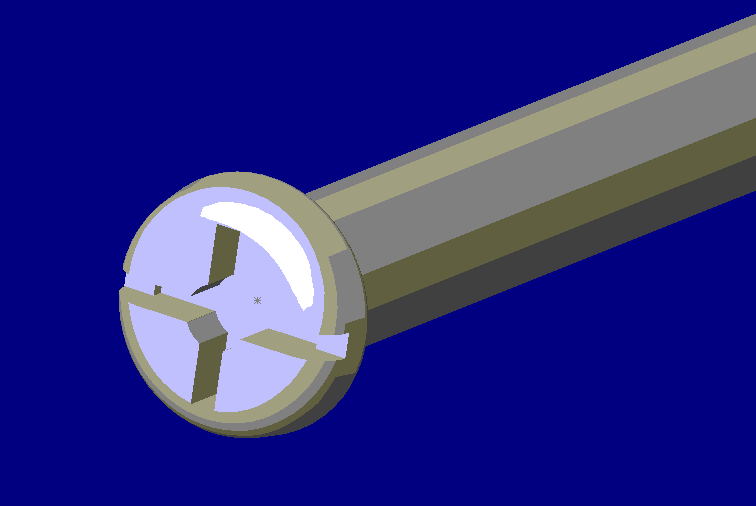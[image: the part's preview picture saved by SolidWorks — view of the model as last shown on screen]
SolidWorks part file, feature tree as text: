
SOLIDWORKS PART (.sldprt)
format: sldprt  version: not decoded by parser v0  size: 270,848 bytes
history: native  units: mm
features: sketch x4, plane x3, extrude x2, fillet x2, cut_extrude x2, material x1, chamfer x1 (+8 scaffold rows collapsed)
feature tree (23):
  scaffold x8  (default folders/planes/origin — collapsed)
  material  "Matériau <non spécifié>"
  plane  "Plane1"
  plane  "Plane2"
  plane  "Plane3"
  sketch  "Esquisse1"  dims[D1=5.0mm]
  extrude  "Base-Extrusion"  Depth=1.5mm
  fillet  "Congé1"  Radius=0.75mm
  fillet  "Congé2"  Radius=0.25mm
  sketch  "Esquisse2"  dims[D1=3.0mm]
  extrude  "Boss.-Extru.1"  Depth=27mm
  chamfer  "Chanfrein1"  Distance=0.5mm Angle=45deg
  sketch  "Esquisse4"  dims[D1=1.25mm D2=0.5mm D3=1.75mm D4=~1.100481mm]
  cut_extrude  "Enlèv. mat.-Extru.1"  Depth=1mm
  sketch  "Esquisse5"
  cut_extrude  "Enlèv. mat.-Extru.2"  Depth=0.75mm
decode coverage: 10 of 11 modeling features carry decoded parameters
note: ~ marks probable driven/reference dimensions
note: suppression state not decoded; provenance and decode notes live in map.json
